# Revit family: LAMP_DOMO 220 G2 (DALI)
name_source: partatom
category: Modelos genéricos
revit_build: Autodesk Revit 2015 (Build: 20140606_1530(x64)
units: mm (PartAtom-declared; Revit-internal decimal feet)

## types (18) — shared parameters
CRI = 80
Diameter = 160 mm  [stored 0.524934 ft]
Elevación por defecto = 1219 mm
Fabricante = LAMP
Finish = Matte white
Gear = Adjustable DALI
Height = 103 mm  [stored 0.337927 ft]
IEE = A+
Installation instructions = http://www.lamp.es
Insulation class = II
Lamp = MID-POWER LED
Last update = 30/06/2020
Luminaire type = Indoor - Recessed Downlight
MacAdam = 3
Manufacturer URL = http://www.lamp.es
Manufacturer country = Spain
Manufacturer name = LAMP
Power Supply = 120-240V 50-60Hz
Product URL = http://www.lamp.es
Product datasheet = http://www.lamp.es
Recessed diameter = 153 mm  [stored 0.501969 ft]
Type = MID POWER NICHIA
Weight = 1.51 kg

## per-type parameters (varying)
| type | Descripción | Efficacy | Initial color | Initial intensity | LED Lifetime | Modelo | Photometric web file | Plum | Power | Product code | Protection rating |
| 2054LM 3000 | DOMO 220 G2 2000 WW DALI | 89 lm/W | 3000 K | 2054 lm | 50.000 L90 B10 | DO2RD20SY830DW | Cuerpo Domo220 : 2054LM 3000 | 23 W | 21 W | DO2RD20SY830DW | IP20 |
| 2136LM 4000 | DOMO 220 G2 2000 NW DALI | 93 lm/W | 4000 K | 2136 lm | 50.000 L90 B10 | DO2RD20SY840DW | Cuerpo Domo220 : 2136LM 4000 | 23 W | 21 W | DO2RD20SY840DW | IP20 |
| 2825LM 3000 | DOMO 220 G2 3000 WW DALI | 88 lm/W | 3000 K | 2825 lm | 50.000 L90 B10 | DO2RD30SY830DW | Cuerpo Domo220 : 2825LM 3000 | 32 W | 29 W | DO2RD30SY830DW | IP20 |
| 2938LM 4000 | DOMO 220 G2 3000 NW DALI | 92 lm/W | 4000 K | 2938 lm | 50.000 L90 B10 | DO2RD30SY840DW | Cuerpo Domo220 : 2938LM 4000 | 32 W | 29 W | DO2RD30SY840DW | IP20 |
| 3665LM 3000 | DOMO 220 G2 4000 WW DALI | 91 lm/W | 3000 K | 3665 lm | 50.000 L80 B10 | DO2RD40SY830DW | Cuerpo Domo220 : 3665LM 3000 | 41 W | 37 W | DO2RD40SY830DW | IP20 |
| 3812LM 4000 | DOMO 220 G2 4000 NW DALI | 94 lm/W | 4000 K | 3812 lm | 50.000 L80 B10 | DO2RD40SY840DW | Cuerpo Domo220 : 3812LM 4000 | 41 W | 37 W | DO2RD40SY840DW | IP20 |
| 1597LM 3000 OPAL GLASS ACC | DOMO 220 G2 2000 WW DALI + DOMO 220 ACC. OPAL GLASS WH. | 69 lm/W | 3000 K | 1597 lm | 50.000 L90 B10 | DO2RD20SY830DW+DIOPRD240W | Cuerpo Domo220 : 1597LM 3000 OPAL GLASS ACC | 23 W | 21 W | DO2RD20SY830DW+DIOPRD240W | IP54 |
| 1484LM 3000 INT OPAL GLASS ACC | DOMO 220 G2 2000 WW DALI + DOMO 220 ACC.TRANSP GLASS WH. | 79 lm/W | 3000 K | 1815 lm | 50.000 L90 B10 | DO2RD20SY830DW+DITRRD240W | Cuerpo Domo220 : 1484LM 3000 INT OPAL GLASS ACC | 23 W | 21 W | DO2RD20SY830DW+DITRRD240W | IP54 |
| 1815LM 3000 GLASS ACC | DOMO 220 G2 2000 NW DALI + DOMO 220 ACC. OPAL GLASS WH. | 72 lm/W | 4000 K | 1661 lm | 50.000 L90 B10 | DO2RD20SY840DW+DIOPRD240W | Cuerpo Domo220 : 1815LM 3000 GLASS ACC | 23 W | 21 W | DO2RD20SY840DW+DIOPRD240W | IP54 |
| 1661LM 4000 OPAL GLASS ACC | DOMO 220 G2 2000 NW DALI + DOMO 220 ACC.TRANSP GLASS WH. | 82 lm/W | 4000 K | 1888 lm | 50.000 L80 B10 | DO2RD20SY840DW+DITRRD240W | Cuerpo Domo220 : 1661LM 4000 OPAL GLASS ACC | 23 W | 21 W | DO2RD20SY840DW+DITRRD240W | IP54 |
| 1544LM 4000 INT OPAL GLASS ACC | DOMO 220 G2 3000 WW DALI + DOMO 220 ACC. OPAL GLASS WH. | 67 lm/W | 3000 K | 2196 lm | 50.000 L90 B10 | DO2RD30SY830DW+DIOPRD240W | Cuerpo Domo220 : 1544LM 4000 INT OPAL GLASS ACC | 32 W | 29 W | DO2RD30SY830DW+DIOPRD240W | IP54 |
| 1888LM 4000 GLASS ACC | DOMO 220 G2 3000 WW DALI + DOMO 220 ACC.TRANSP GLASS WH. | 76 lm/W | 3000 K | 2497 lm | 50.000 L90 B10 | DO2RD30SY830DW+DITRRD240W | Cuerpo Domo220 : 1888LM 4000 GLASS ACC | 32 W | 29 W | DO2RD30SY830DW+DITRRD240W | IP54 |
| 2196LM 3000 OPAL GLASS ACC | DOMO 220 G2 3000 NW DALI+ DOMO 220 ACC. OPAL GLASS WH. | 69 lm/W | 4000 K | 2284 lm | 50.000 L90 B10 | DO2RD30SY840DW+DIOPRD240W | Cuerpo Domo220 : 2196LM 3000 OPAL GLASS ACC | 32 W | 29 W | DO2RD30SY840DW+DIOPRD240W | IP54 |
| 2042LM 3000 INT OPAL GLASS ACC | DOMO 220 G2 3000 NW DALI + DOMO 220 ACC.TRANSP GLASS WH. | 79 lm/W | 4000 K | 2597 lm | 50.000 L80 B10 | DO2RD30SY840DW+DITRRD240W | Cuerpo Domo220 : 2042LM 3000 INT OPAL GLASS ACC | 32 W | 29 W | DO2RD30SY840DW+DITRRD240W | IP54 |
| 2497LM 3000 GLASS ACC | DOMO 220 G2 4000 WW DALI + DOMO 220 ACC. OPAL GLASS WH. | 68 lm/W | 3000 K | 2849 lm | 50.000 L90 B10 | DO2RD40SY830DW+DIOPRD240W | Cuerpo Domo220 : 2497LM 3000 GLASS ACC | 41 W | 37 W | DO2RD40SY830DW+DIOPRD240W | IP54 |
| 2284LM 4000 OPAL GLASS ACC | DOMO 220 G2 4000 WW DALI + DOMO 220 ACC.TRANSP GLASS WH. | 77 lm/W | 3000 K | 3239 lm | 50.000 L90 B10 | DO2RD40SY830DW+DITRRD240W | Cuerpo Domo220 : 2284LM 4000 OPAL GLASS ACC | 41 W | 37 W | DO2RD40SY830DW+DITRRD240W | IP54 |
| 2123LM 4000 INT OPAL GLASS ACC | DOMO 220 G2 4000 NW DALI + DOMO 220 ACC. OPAL GLASS WH. | 71 lm/W | 4000 K | 2963 lm | 50.000 L90 B10 | DO2RD40SY840DW+DIOPRD240W | Cuerpo Domo220 : 2123LM 4000 INT OPAL GLASS ACC | 41 W | 37 W | DO2RD40SY840DW+DIOPRD240W | IP54 |
| 2597LM 4000 GLASS ACC | DOMO 220 G2 4000 NW DALI + DOMO 220 ACC.TRANSP GLASS WH. | 80 lm/W | 4000 K | 3369 lm | 50.000 L80 B10 | DO2RD40SY840DW+DITRRD240W | Cuerpo Domo220 : 2597LM 4000 GLASS ACC | 41 W | 37 W | DO2RD40SY840DW+DITRRD240W | IP54 |

note: [stored X ft] marks values corroborated as IEEE doubles in the binary element streams (Revit-internal decimal feet)
